# Revit family: NBS_AirflowDevelopmentsLtd_AirHdlngUnits_DuplexventDV_SideEntry
name_source: partatom
category: Mechanical Equipment
revit_build: Autodesk Revit 2013 (Build: 20121003_2115(x64)
units: mm (PartAtom-declared; Revit-internal decimal feet)

## types (2) — shared parameters
AirHandlerConstruction = MANUFACTUREDITEM
AirHandlerFanCoilArrangement = DRAWTHROUGH
AirductRearLeft1Horizontal = 96 mm  [stored 0.314961 ft]
AirductRearRight1Horizontal = 96 mm  [stored 0.314961 ft]
AssetType = Fixed
CasingInsulation = 20 mm
CodePerformance = Complies with NHBC criteria and ErP 2013/2015 standards, meets Building Regulations Approved Document F
ComponentsAttenuators = Acoustic lining
ComponentsFans = EC fans
ComponentsFilters = Triple panel filter (2 x G4, 1 x F7)
ComponentsReHeaters = 900 W electric heater
Construction = Double skin
ControlBoxMaterial = NBS_Concept
DV50L = No
DV580L = No
DigitalControl = Optional Extra
DirectionOfAirflow = Horizontal
DualDeck = No
DuctMaterial = NBS_Concept
DurationUnit = year
DutyExternalResistance = 100 Pa
Environment = Internal
Features = Triple filter design with F7 pollen filter, greater than 90% heat recovery efficiency, low SPF, low energy and maintenance EC fans, off-the-shelf delivery, low noise, 4 speed control, multi-spigot design for installation flexibility
HasProtectiveEarth = No
HeatRecoveryEfficiency = >90%
IfcExportAs = IfcUnitaryEquipmentType
IfcExportType = AIRHANDLER
InstallationOptions = Ceiling hung, floor standing
InsulationStandardClass = Unset
ManufacturerName = Airflow Developments Ltd
ManufacturerURL = www.airflow.com
Material = Galvanised steel casing
NBSDescription = Air handling units
NBSReference = 90-45-15/310
NominalFrequencyRange = 0.0 , 0.0
NominalVoltage = 230.0 , 230.0
OptionalControls = Humidity, CO2 sensors
PhaseAngle = 0.00°
PositionsForMaintenenceAccess = Removable front panel
ProtectionClass = IP34
Shape = Rectangular
TemperatureRegulators = Automatic summer bypass, frost protection heater
Uniclass2 = 90-04-03/408
UnitMaterial = NBS_Concept
Uses = Residential
Version = 1
WarrantyDurationParts = 7
WarrantyDurationUnit = year
zero-valued in all types: NominalCurrent, NumberOfPoles, ThermalEfficiency, UnitWeight, UsageCurrent

## per-type parameters (varying)
- DV50R: AccessoryOptions=Airflex Pro ducting system, 4-speed selection switch, summer bypass damper switch, a range of air heaters, in-line silencers, floor, wall and ceiling inlet and outlet diffusers,; AirDuctInnerRadius=50 mm  [stored 0.164042 ft]; AirDuctRadius=53 mm; AirductLeft1Horizontal=87 mm  [stored 0.285433 ft]; AirductLeft2Horizontal=197 mm; AirductRearLeft2Horizontal=206 mm  [stored 0.675853 ft]; AirductRearRight2Horizontal=206 mm  [stored 0.675853 ft]; AirductRight1Horizontal=87 mm  [stored 0.285433 ft]; AirductRight2Horizontal=197 mm; AirductSide1Vertical=86 mm  [stored 0.282152 ft]; AirductSide2Vertcial=161 mm  [stored 0.528215 ft]; BIMObjectName=NBS_AirflowDevelopmentsLtd_AirHandlingUnits_DV50; ComponentsHeatRecovery=Counter flow, aluminium; DV50R=Yes; DV80R=No; Description=MVHR unit for use in small sized dwellings up to 100m², with a maximum extraction of 216 m³/h @ 100 Pa; DutyAirVolume=230 m³/h max. (216 m³/h @ 100 Pa); DutySoundPowerLevel=49 dB(A); ElectricalDeviceNominalPower=104; ModelNumber=90000003; ModelReference=Duplexvent DV50; NBSCertification=www.nationalbimlibrary.com/airflow-developments-ltd/duplexvent-dv50; Name=AirHandlingUnits_DuplexventDV50_AirflowDevelopmentsLtd; NominalHeight=236 mm; NominalLength=900 mm  [stored 2.95276 ft]; NominalWidth=546 mm  [stored 1.79134 ft]; ProductInformation=www.airflow.com/productdetail_/pg_VUNI/90000003; Size=900 x 547 x 236 mm; SustainabilityPerformance=Passive House Institute certified, SAP Appendix Q eligible up to K+4; UnitHeight=236 mm; UnitLength=900 mm  [stored 2.95276 ft]; UnitWidth=546 mm  [stored 1.79134 ft]
- DV80R: AccessoryOptions=Airflex Pro ducting system, 4-speed selection switch, summer bypass damper switch, a range of air heaters, in-line silencers, floor, wall and ceiling inlet and outlet diffusers; AirDuctInnerRadius=63 mm; AirDuctRadius=65 mm  [stored 0.213255 ft]; AirductLeft1Horizontal=111 mm; AirductLeft2Horizontal=255 mm  [stored 0.836614 ft]; AirductRearLeft2Horizontal=231 mm  [stored 0.757874 ft]; AirductRearRight2Horizontal=231 mm  [stored 0.757874 ft]; AirductRight1Horizontal=111 mm; AirductRight2Horizontal=255 mm  [stored 0.836614 ft]; AirductSide1Vertical=200 mm  [stored 0.656168 ft]; AirductSide2Vertcial=111 mm; BIMObjectName=NBS_AirflowDevelopmentsLtd_AirHandlingUnits_DV80; ComponentsHeatRecovery=Counter flow, plastic; DV50R=No; DV80R=Yes; Description=MVHR unit for use in medium sized dwellings up to 180m², with a maximum extraction of 342 m³/h @ 100 Pa; DutyAirVolume=360 m³/h max. (342 m³/h @ 100 Pa); DutySoundPowerLevel=48 dB(A); ElectricalDeviceNominalPower=165; ModelNumber=0000067; ModelReference=Duplexvent DV80; NBSCertification=www.nationalbimlibrary.com/airflow-developments-ltd/duplexvent-dv80; Name=AirHandlingUnits_DuplexventDV80_AirflowDevelopmentsLtd; NominalHeight=295 mm  [stored 0.967848 ft]; NominalLength=1026 mm  [stored 3.36614 ft]; NominalWidth=624 mm  [stored 2.04724 ft]; ProductInformation=www.airflow.com/productdetail_/pg_VUNI/90000067; Size=1026 x 626 x 293 mm; SustainabilityPerformance=Passive House Institute certified, SAP Appendix Q eligible up to K+6; UnitHeight=295 mm  [stored 0.967848 ft]; UnitLength=1026 mm  [stored 3.36614 ft]; UnitWidth=624 mm  [stored 2.04724 ft]

note: [stored X ft] marks values corroborated as IEEE doubles in the binary element streams (Revit-internal decimal feet)

## geometry (parser evidence)
native form markers: Sweep x2
no freeform markers — native parametric forms only
